SOLIDWORKS PART (.sldprt)
format: sldprt  version: not decoded by parser v0  size: 267,776 bytes
history: native  units: mm
features: sketch x9, plane x3, material x1, mirror x1, extrude x1 (+11 scaffold rows collapsed)
feature tree (26):
  scaffold x11  (default folders/planes/origin — collapsed)
  material  "Material <not specified>"
  sketch  "Sketch1"  dims[c1.D1=914.4mm c1.D2=12.7mm c1.D3=~49.242289mm c2.D3=120.0deg c2.D4=101.6mm c2.D5=101.6mm]
  sketch  "3DSketch1"  dims[D1=6.35mm D2=44.45mm]
  plane  "Plane1"
  plane  "Plane2"
  sketch  "Sketch2"  dims[D2=203.2mm D3=152.4mm D1=50.8mm D4=114.3mm]
  sketch  "Sketch3"  dims[D1=254.0mm D2=177.8mm]
  sketch  "Sketch4"  dims[D1=12.7mm D2=203.2mm]
  sketch  "Sketch5"
  sketch  "Sketch6"
  mirror  "Mirror1"
  sketch  "Sketch17"  dims[c1.D1=44.45mm c2.D1=~2.392344deg c3.D1=254.0mm c3.D2=304.8mm c3.D3=~61.669386mm c4.D2=304.8mm c4.D3=298.45mm c4.D4=~973.058787mm c4.D5=596.9mm c4.D1=330.2mm c5.D2=76.2mm c5.D6=911.86mm c5.D4=~96.556238mm c5.D7=~96.556238mm]
  extrude  "Boss-Extrude2"  Depth=6.35mm
  plane  "Plane5"  Offset=100.33mm
  sketch  "Sketch14"
decode coverage: 7 of 11 modeling features carry decoded parameters
note: ~ marks probable driven/reference dimensions
note: suppression state not decoded; provenance and decode notes live in map.json
